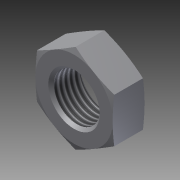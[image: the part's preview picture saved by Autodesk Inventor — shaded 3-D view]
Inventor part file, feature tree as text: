
AUTODESK INVENTOR PART (.ipt)
format: ipt  version: 2012 (Build 160160000, 160)  size: 145,408 bytes
history: native  units: in
note: dims shown in document units (in); Inventor stores cm internally (conversion verified against a paired STEP export)
features: other x70, sketch x3, revolve x2, extrude x1, thread x1
ambient origin geometry x8: Origin, YZ Plane, XZ Plane, XY Plane, X Axis, Y Axis, Z Axis, Center Point
bodies: Solid1 (feature_tree)
feature tree (77):
  sketch  "Sketch_8"  dims[d0=360.0deg d1=0.31in d2=0.0in]
  sketch  "Sketch_10"  dims[d3=360.0deg d4=0.2559in d5=0.0in]
  revolve  "Revolution1"  [1 undecoded]
  extrude  "Extrusion1"  Depth=0.2559in TaperAngle=0.0deg
  revolve  "Revolution2"  [1 undecoded]
  thread  "Thread1"  [1 undecoded]
  other  "NUT_XY"
  other  "NUT_YZ"
  other  "NUT_ZX"
  other  "NUT_X"
  other  "NUT_Y"
  other  "NUT_Z"
  other  "NUT_Center"
  other  "a1_XY"
  other  "a1_YZ"
  other  "a1_ZX"
  other  "a1_X"
  other  "a1_Y"
  other  "a1_Z"
  other  "a1_Center"
  other  "a2_XY"
  other  "a2_YZ"
  other  "a2_ZX"
  other  "a2_X"
  other  "a2_Y"
  other  "a2_Z"
  other  "a2_Center"
  other  "b1_XY"
  other  "b1_YZ"
  other  "b1_ZX"
  other  "b1_X"
  other  "b1_Y"
  other  "b1_Z"
  other  "b1_Center"
  other  "b2_XY"
  other  "b2_YZ"
  other  "b2_ZX"
  other  "b2_X"
  other  "b2_Y"
  other  "b2_Z"
  other  "b2_Center"
  other  "e_XY"
  other  "e_YZ"
  other  "e_ZX"
  other  "e_X"
  other  "e_Y"
  other  "e_Z"
  other  "e_Center"
  other  "th1_XY"
  other  "th1_YZ"
  other  "th1_ZX"
  other  "th1_X"
  other  "th1_Y"
  other  "th1_Z"
  other  "th1_Center"
  other  "th2_XY"
  other  "th2_YZ"
  other  "th2_ZX"
  other  "th2_X"
  other  "th2_Y"
  other  "th2_Z"
  other  "th2_Center"
  other  "ol1_XY"
  other  "ol1_YZ"
  other  "ol1_ZX"
  other  "ol1_X"
  other  "ol1_Y"
  other  "ol1_Z"
  other  "ol1_Center"
  other  "ol2_XY"
  other  "ol2_YZ"
  other  "ol2_ZX"
  other  "ol2_X"
  other  "ol2_Y"
  other  "ol2_Z"
  other  "ol2_Center"
  sketch  "Sketch_11"
note: 3 required parameter values undecoded (feature->parameter linkage not recoverable at this tier; creation-order binding heuristic only, values carry confidence <= 0.55)